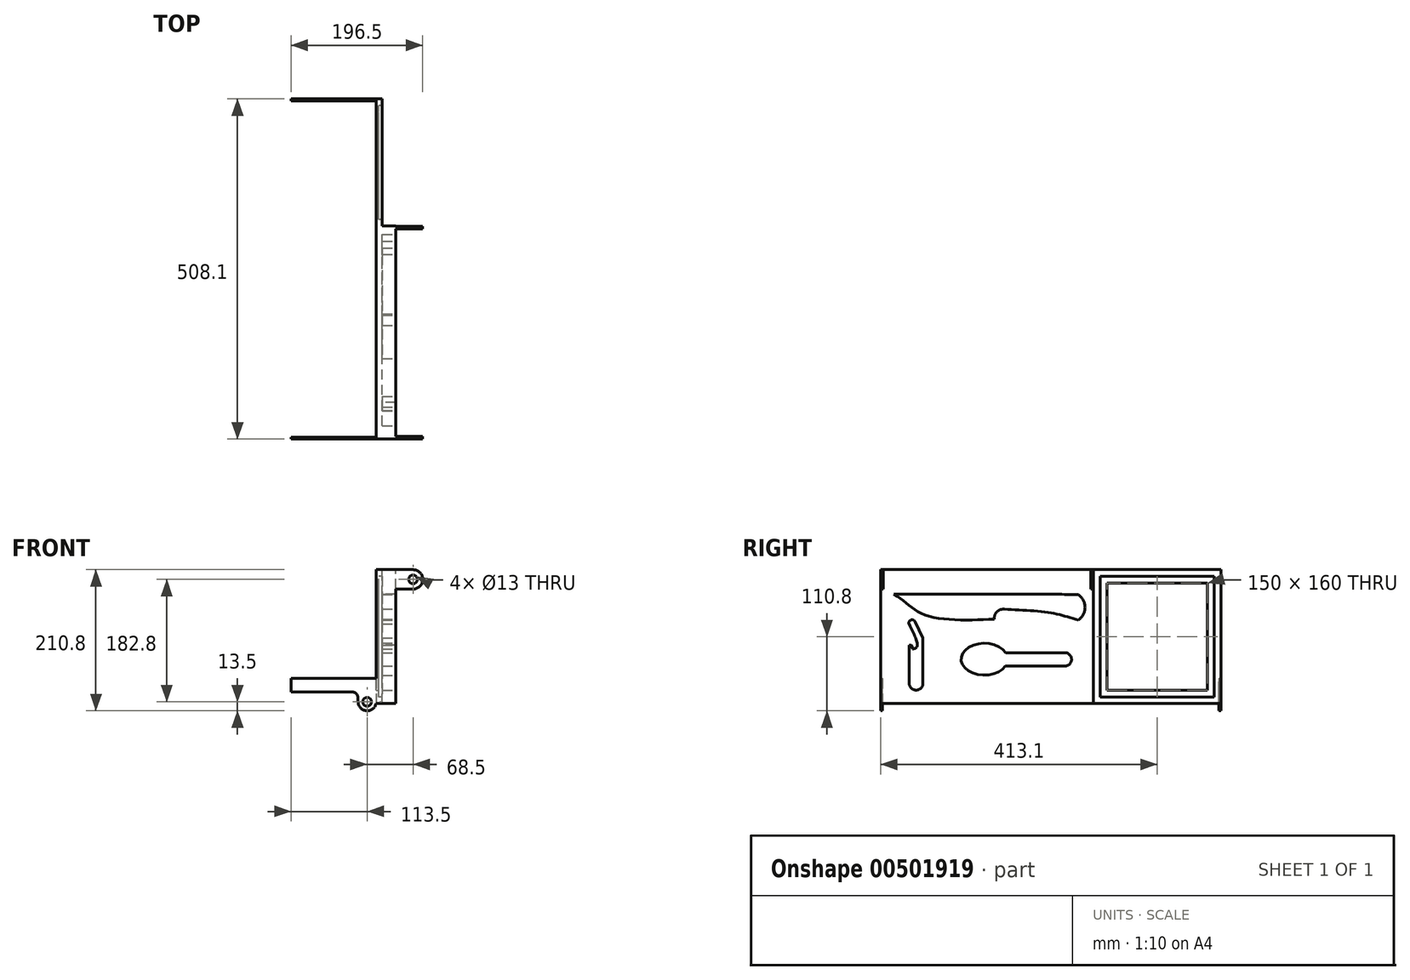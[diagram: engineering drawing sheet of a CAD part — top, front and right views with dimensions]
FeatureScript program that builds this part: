
annotation { "Feature Type Name" : "Feature", "Feature Type Description" : "" }
export const myFeature = defineFeature(function(context is Context, id is Id, definition is map)
    precondition{}
    {
        {
            var Q0;
            Q0=qCreatedBy(makeId("Front.planeOp"),FACE);
            var sketch = newSketch(context, id + "F0", { "sketchPlane" : qUnion([Q0])});
            skArc(sketch, "E0", {"start": v(-13.5, 0) * mm, "mid": v(-1.36, -13.43) * mm, "end": v(13.23, -2.7) * mm});
            skLineSegment(sketch, "E1.left", {"start": v(-13.5, 0) * mm, "end": v(-13.5, 15) * mm});
            skLineSegment(sketch, "E1.right", {"start": v(13.5, -2.7) * mm, "end": v(13.5, 15) * mm});
            skLineSegment(sketch, "E2.trimOffspring", {"start": v(13.23, -2.7) * mm, "end": v(13.5, -2.7) * mm});
            skLineSegment(sketch, "E3.bottom", {"start": v(-13.5, 15) * mm, "end": v(-113.5, 15) * mm});
            skLineSegment(sketch, "E3.top", {"start": v(13.5, 35) * mm, "end": v(-113.5, 35) * mm});
            skLineSegment(sketch, "E3.left", {"start": v(13.5, 15) * mm, "end": v(13.5, 35) * mm});
            skLineSegment(sketch, "E3.right", {"start": v(-113.5, 15) * mm, "end": v(-113.5, 35) * mm});
            skPoint(sketch, "E4.start.orphan", {"position": v(-6.5, 0) * mm});
            skPoint(sketch, "E5.end.orphan", {"position": v(6.5, 0) * mm});
            skCircle(sketch, "E6", {"center": v(0, 0) * mm, "radius": 6.5 * mm});
            skSolve(sketch);
        }
        {
            var Q0;
            Q0=makeQuery(id+"F0.imprint","IMPRINT",FACE,{"disambiguationData":[TD([[makeQuery(id+"F0.imprint","IMPRINT",EDGE,{"derivedFrom":sQuery(id+"F0.wireOp",EDGE,"E0")}),1.0]])]});
            extrude(context, id + "F1", {"entities" : qUnion([Q0]), "endBound" : BoundingType.SYMMETRIC, "depth" : 508.1 * mm});
        }
        {
            var Q0;
            Q0=makeQuery(id+"F1.opExtrude","SWEPT_FACE",FACE,{"disambiguationData":[OSD([sQuery(id+"F0.wireOp",EDGE,"E1.right"),sQuery(id+"F0.wireOp",EDGE,"E3.left")])]});
            var sketch = newSketch(context, id + "F2", { "sketchPlane" : qUnion([Q0])});
            skLineSegment(sketch, "E7.bottom", {"start": v(-251.05, 50) * mm, "end": v(251.05, 50) * mm});
            skLineSegment(sketch, "E7.top", {"start": v(-251.05, -50) * mm, "end": v(251.05, -50) * mm});
            skLineSegment(sketch, "E7.left", {"start": v(-251.05, 50) * mm, "end": v(-251.05, -50) * mm});
            skLineSegment(sketch, "E7.right", {"start": v(251.05, 50) * mm, "end": v(251.05, -50) * mm});
            skPoint(sketch, "E7.middle", {"position": v(0, 0) * mm});
            skSolve(sketch);
        }
        {
            var Q0;
            Q0=qSketchRegion(id+"F2",true);
            extrude(context, id + "F3", {"entities" : qUnion([Q0]), "operationType" : NewBodyOperationType.REMOVE, "oppositeDirection" : true, "depth" : 140 * mm});
        }
        {
            var Q0;
            {var subQ0=sQuery(id+"F0.wireOp",EDGE,"E3.bottom");var subQ1=sQuery(id+"F0.wireOp",EDGE,"E1.left");Q0=makeQuery(id+"F3.boolean.opBoolean","SPLIT",EDGE,{"disambiguationData":[TD([makeQuery(id+"F3.opExtrude","SWEPT_FACE",FACE,{"disambiguationData":[OSD([sQuery(id+"F2.wireOp",EDGE,"E7.left")])]})])],"derivedFrom":makeQuery(id+"F1.opExtrude","SWEPT_EDGE",EDGE,{"disambiguationData":[OSD([subQ1,subQ0])]})});}
            var Q1;
            {var subQ0=sQuery(id+"F0.wireOp",EDGE,"E3.bottom");var subQ1=sQuery(id+"F0.wireOp",EDGE,"E1.left");Q1=makeQuery(id+"F3.boolean.opBoolean","SPLIT",EDGE,{"disambiguationData":[TD([makeQuery(id+"F3.opExtrude","SWEPT_FACE",FACE,{"disambiguationData":[OSD([sQuery(id+"F2.wireOp",EDGE,"E7.right")])]})])],"derivedFrom":makeQuery(id+"F1.opExtrude","SWEPT_EDGE",EDGE,{"disambiguationData":[OSD([subQ1,subQ0])]})});}
            fillet(context, id + "F4", {"entities" : qUnion([Q0, Q1]), "radius" : 10 * mm, "tangentPropagation" : true, "allowEdgeOverflow" : false});
        }
        {
            var Q0;
            {var subQ0=sQuery(id+"F0.wireOp",EDGE,"E3.left");var subQ3=sQuery(id+"F0.wireOp",EDGE,"E1.right");Q0=makeQuery(id+"F3.boolean.opBoolean","SPLIT",FACE,{"disambiguationData":[TD([makeQuery(id+"F3.opExtrude","SWEPT_FACE",FACE,{"disambiguationData":[OSD([sQuery(id+"F2.wireOp",EDGE,"E7.left")])]})])],"derivedFrom":makeQuery(id+"F1.opExtrude","SWEPT_FACE",FACE,{"disambiguationData":[OSD([subQ3,subQ0])]})});}
            var sketch = newSketch(context, id + "F5", { "sketchPlane" : qUnion([Q0])});
            skLineSegment(sketch, "E8.bottom", {"start": v(-254.05, -2.7) * mm, "end": v(254.05, -2.7) * mm});
            skLineSegment(sketch, "E8.top", {"start": v(-254.05, 197.3) * mm, "end": v(254.05, 197.3) * mm});
            skLineSegment(sketch, "E8.left", {"start": v(-254.05, -2.7) * mm, "end": v(-254.05, 197.3) * mm});
            skLineSegment(sketch, "E8.right", {"start": v(254.05, -2.7) * mm, "end": v(254.05, 197.3) * mm});
            skSolve(sketch);
        }
        {
            var Q0;
            Q0=qSketchRegion(id+"F5",true);
            extrude(context, id + "F6", {"entities" : qUnion([Q0]), "operationType" : NewBodyOperationType.ADD, "depth" : 4 * mm});
        }
        {
            var Q0;
            Q0=makeQuery(id+"F6.opExtrude","CAP_FACE",FACE,{"disambiguationData":[OSD([sQuery(id+"F5.wireOp",EDGE,"E8.bottom"),sQuery(id+"F5.wireOp",EDGE,"E8.top"),sQuery(id+"F5.wireOp",EDGE,"E8.left"),sQuery(id+"F5.wireOp",EDGE,"E8.right")])],"isStart":false});
            var sketch = newSketch(context, id + "F7", { "sketchPlane" : qUnion([Q0])});
            skLineSegment(sketch, "E9.bottom", {"start": v(84.05, 17.3) * mm, "end": v(234.05, 17.3) * mm});
            skLineSegment(sketch, "E9.top", {"start": v(84.05, 177.3) * mm, "end": v(234.05, 177.3) * mm});
            skLineSegment(sketch, "E9.left", {"start": v(84.05, 17.3) * mm, "end": v(84.05, 177.3) * mm});
            skLineSegment(sketch, "E9.right", {"start": v(234.05, 17.3) * mm, "end": v(234.05, 177.3) * mm});
            skSolve(sketch);
        }
        {
            var Q0;
            Q0 = qSketchRegion(id + "F7", true);
            extrude(context, id + "F8", {"entities" : qUnion([Q0]), "operationType" : NewBodyOperationType.REMOVE, "oppositeDirection" : true, "depth" : 25 * mm});
        }
        {
            var Q0;
            Q0=makeQuery(id+"F6.opExtrude","CAP_FACE",FACE,{"disambiguationData":[OSD([sQuery(id+"F5.wireOp",EDGE,"E8.bottom"),sQuery(id+"F5.wireOp",EDGE,"E8.top"),sQuery(id+"F5.wireOp",EDGE,"E8.left"),sQuery(id+"F5.wireOp",EDGE,"E8.right")])],"isStart":false});
            var sketch = newSketch(context, id + "F9", { "sketchPlane" : qUnion([Q0])});
            skLineSegment(sketch, "E10.bottom", {"start": v(254.05, -2.7) * mm, "end": v(64.05, -2.7) * mm});
            skLineSegment(sketch, "E10.top", {"start": v(254.05, 197.3) * mm, "end": v(64.05, 197.3) * mm});
            skLineSegment(sketch, "E10.left", {"start": v(254.05, -2.7) * mm, "end": v(254.05, 197.3) * mm});
            skLineSegment(sketch, "E10.right", {"start": v(64.05, -2.7) * mm, "end": v(64.05, 197.3) * mm});
            skSolve(sketch);
        }
        {
            var Q0;
            Q0 = qSketchRegion(id + "F9", true);
            extrude(context, id + "F10", {"entities" : qUnion([Q0]), "operationType" : NewBodyOperationType.ADD, "depth" : 5 * mm});
        }
        {
            var Q0;
            Q0=makeQuery(id+"F9.imprint","IMPRINT",FACE,{"disambiguationData":[TD([[makeQuery(id+"F9.imprint","IMPRINT",EDGE,{"derivedFrom":sQuery(id+"F9.wireOp",EDGE,"E10.bottom")}),1.0]])]});
            var sketch = newSketch(context, id + "F11", { "sketchPlane" : qUnion([Q0])});
            skLineSegment(sketch, "E11.bottom", {"start": v(74.05, 7.3) * mm, "end": v(244.05, 7.3) * mm});
            skLineSegment(sketch, "E11.top", {"start": v(74.05, 187.3) * mm, "end": v(244.05, 187.3) * mm});
            skLineSegment(sketch, "E11.left", {"start": v(74.05, 7.3) * mm, "end": v(74.05, 187.3) * mm});
            skLineSegment(sketch, "E11.right", {"start": v(244.05, 7.3) * mm, "end": v(244.05, 187.3) * mm});
            skSolve(sketch);
        }
        {
            var Q0;
            Q0 = qSketchRegion(id + "F11", true);
            extrude(context, id + "F12", {"entities" : qUnion([Q0]), "operationType" : NewBodyOperationType.REMOVE, "depth" : 25 * mm});
        }
        {
            var Q0;
            Q0=makeQuery(id+"F6.opExtrude","CAP_FACE",FACE,{"disambiguationData":[OSD([sQuery(id+"F5.wireOp",EDGE,"E8.bottom"),sQuery(id+"F5.wireOp",EDGE,"E8.top"),sQuery(id+"F5.wireOp",EDGE,"E8.left"),sQuery(id+"F5.wireOp",EDGE,"E8.right")])],"isStart":false});
            var sketch = newSketch(context, id + "F13", { "sketchPlane" : qUnion([Q0])});
            skLineSegment(sketch, "E12.bottom", {"start": v(-254.05, -2.7) * mm, "end": v(64.05, -2.7) * mm});
            skLineSegment(sketch, "E12.top", {"start": v(-254.05, 197.3) * mm, "end": v(64.05, 197.3) * mm});
            skLineSegment(sketch, "E12.left", {"start": v(-254.05, -2.7) * mm, "end": v(-254.05, 197.3) * mm});
            skLineSegment(sketch, "E12.right", {"start": v(64.05, -2.7) * mm, "end": v(64.05, 197.3) * mm});
            skSolve(sketch);
        }
        {
            var Q0;
            Q0 = qSketchRegion(id + "F13", true);
            extrude(context, id + "F14", {"entities" : qUnion([Q0]), "operationType" : NewBodyOperationType.ADD, "depth" : 25 * mm});
        }
        {
            var Q0;
            Q0=makeQuery(id+"F14.opExtrude","CAP_FACE",FACE,{"disambiguationData":[OSD([sQuery(id+"F13.wireOp",EDGE,"E12.bottom"),sQuery(id+"F13.wireOp",EDGE,"E12.top"),sQuery(id+"F13.wireOp",EDGE,"E12.left"),sQuery(id+"F13.wireOp",EDGE,"E12.right")])],"isStart":false});
            var sketch = newSketch(context, id + "F15", { "sketchPlane" : qUnion([Q0])});
            skLineSegment(sketch, "E13", {"start": v(-234.06, 160.84) * mm, "end": v(-42.72, 160.84) * mm});
            skFitSpline(sketch, "E14", {"points": [v(-234.06, 160.84) * mm, v(-190.52, 130.77) * mm, v(-84.33, 123.56) * mm], "startDerivative": vector(123, -69.12) * mm, "endDerivative": vector(178.86, 10.6) * mm});
            skArc(sketch, "E15", {"start": v(-69.13, 138.37) * mm, "mid": v(-80.08, 134.4) * mm, "end": v(-84.33, 123.56) * mm});
            skFitSpline(sketch, "E16", {"points": [v(-69.13, 138.37) * mm, v(0, 132.93) * mm, v(41.5, 122.18) * mm], "startDerivative": vector(118.54, -7.26) * mm, "endDerivative": vector(102.56, -27.5) * mm});
            skArc(sketch, "E17", {"start": v(41.5, 122.18) * mm, "mid": v(51.42, 141) * mm, "end": v(41.5, 159.82) * mm});
            skFitSpline(sketch, "E18", {"points": [v(-42.72, 160.84) * mm, v(0, 160.84) * mm, v(41.5, 159.82) * mm], "startDerivative": vector(93.42, 0.52) * mm, "endDerivative": vector(74.55, -2.22) * mm});
            skEllipticalArc(sketch, "E19", {});
            skLineSegment(sketch, "E20.bottom", {"start": v(21.55, 73.4) * mm, "end": v(-67.06, 73.4) * mm});
            skLineSegment(sketch, "E20.top", {"start": v(21.16, 53.32) * mm, "end": v(-67.45, 53.32) * mm});
            skArc(sketch, "E21", {"start": v(21.16, 53.32) * mm, "mid": v(31.2, 63.17) * mm, "end": v(21.55, 73.4) * mm});
            skLineSegment(sketch, "E22.left", {"start": v(-190.6, 27.77) * mm, "end": v(-190.6, 78.62) * mm});
            skLineSegment(sketch, "E22.right", {"start": v(-211.16, 27.77) * mm, "end": v(-211.16, 78.62) * mm});
            skPoint(sketch, "E22.middle", {"position": v(-200.88, 53.2) * mm});
            skArc(sketch, "E23", {"start": v(-211.16, 27.77) * mm, "mid": v(-200.88, 17.48) * mm, "end": v(-190.6, 27.77) * mm});
            skLineSegment(sketch, "E24", {"start": v(-190.6, 78.62) * mm, "end": v(-190.6, 95.2) * mm});
            skLineSegment(sketch, "E25", {"start": v(-190.6, 95.2) * mm, "end": v(-202.45, 119.74) * mm});
            skLineSegment(sketch, "E26", {"start": v(-211.16, 78.62) * mm, "end": v(-211.16, 84.5) * mm});
            skFitSpline(sketch, "E27", {"points": [v(-206.3, 78.62) * mm, v(-199.26, 82.66) * mm, v(-211.44, 116.07) * mm], "startDerivative": vector(28.24, 6.55) * mm, "endDerivative": vector(-31.47, 61.86) * mm});
            skFitSpline(sketch, "E28", {"points": [v(-211.16, 84.5) * mm, v(-207.87, 84.5) * mm, v(-206.3, 78.62) * mm], "startDerivative": vector(8.84, 2.16) * mm, "endDerivative": vector(1.25, -13.15) * mm});
            skArc(sketch, "E29", {"start": v(-202.45, 119.74) * mm, "mid": v(-208.66, 122.13) * mm, "end": v(-211.44, 116.07) * mm});
            const initialGuessF15  = {"E19": [-0.09883789050244385, 0.06364599973239364, 1, 0, 0.03481733814341265, 0.02387090292371184, 0.4207699255388472, 5.835743280041866]};
            skSetInitialGuess(sketch, initialGuessF15);
            skSolve(sketch);
        }
        {
            var Q0;
            Q0 = qSketchRegion(id + "F15", true);
            extrude(context, id + "F16", {"entities" : qUnion([Q0]), "operationType" : NewBodyOperationType.REMOVE, "oppositeDirection" : true, "depth" : 20 * mm});
        }
        {
            var Q0;
            Q0=makeQuery(id+"F14.boolean.opBoolean","MERGE",FACE,{"derivedFrom":[makeQuery(id+"F6.boolean.opBoolean","MERGE",FACE,{"derivedFrom":[makeQuery(id+"F1.opExtrude","CAP_FACE",FACE,{"disambiguationData":[OSD([sQuery(id+"F0.wireOp",EDGE,"E0"),sQuery(id+"F0.wireOp",EDGE,"E1.left"),sQuery(id+"F0.wireOp",EDGE,"E1.right"),sQuery(id+"F0.wireOp",EDGE,"E2.trimOffspring"),sQuery(id+"F0.wireOp",EDGE,"E3.bottom"),sQuery(id+"F0.wireOp",EDGE,"E3.top"),sQuery(id+"F0.wireOp",EDGE,"E3.left"),sQuery(id+"F0.wireOp",EDGE,"E3.right"),sQuery(id+"F0.wireOp",EDGE,"E6")])],"isStart":false}),makeQuery(id+"F6.opExtrude","SWEPT_FACE",FACE,{"disambiguationData":[OSD([sQuery(id+"F5.wireOp",EDGE,"E8.left")])]})]}),makeQuery(id+"F14.opExtrude","SWEPT_FACE",FACE,{"disambiguationData":[OSD([sQuery(id+"F13.wireOp",EDGE,"E12.left")])]})]});
            var sketch = newSketch(context, id + "F17", { "sketchPlane" : qUnion([Q0])});
            skLineSegment(sketch, "E30.bottom", {"start": v(42.5, 197.3) * mm, "end": v(68.5, 197.3) * mm});
            skLineSegment(sketch, "E30.top", {"start": v(42.5, 168.3) * mm, "end": v(68.5, 168.3) * mm});
            skLineSegment(sketch, "E30.left", {"start": v(42.5, 197.3) * mm, "end": v(42.5, 168.3) * mm});
            skArc(sketch, "E31", {"start": v(68.5, 168.3) * mm, "mid": v(83, 182.8) * mm, "end": v(68.5, 197.3) * mm});
            skCircle(sketch, "E32", {"center": v(68.5, 182.8) * mm, "radius": 6.5 * mm});
            skSolve(sketch);
        }
        {
            var Q0;
            Q0 = qSketchRegion(id + "F17", true);
            extrude(context, id + "F18", {"entities" : qUnion([Q0]), "operationType" : NewBodyOperationType.ADD, "oppositeDirection" : true, "depth" : 318 * mm});
        }
        {
            var Q0;
            Q0=makeQuery(id+"F18.boolean.opBoolean","MERGE",FACE,{"derivedFrom":[makeQuery(id+"F14.boolean.opBoolean","MERGE",FACE,{"derivedFrom":[makeQuery(id+"F10.boolean.opBoolean","MERGE",FACE,{"derivedFrom":[makeQuery(id+"F6.opExtrude","SWEPT_FACE",FACE,{"disambiguationData":[OSD([sQuery(id+"F5.wireOp",EDGE,"E8.top")])]}),makeQuery(id+"F10.opExtrude","SWEPT_FACE",FACE,{"disambiguationData":[OSD([sQuery(id+"F9.wireOp",EDGE,"E10.top")])]})]}),makeQuery(id+"F14.opExtrude","SWEPT_FACE",FACE,{"disambiguationData":[OSD([sQuery(id+"F13.wireOp",EDGE,"E12.top")])]})]}),makeQuery(id+"F18.opExtrude","SWEPT_FACE",FACE,{"disambiguationData":[OSD([sQuery(id+"F17.wireOp",EDGE,"E30.bottom")])]})]});
            var sketch = newSketch(context, id + "F19", { "sketchPlane" : qUnion([Q0])});
            skLineSegment(sketch, "E33.bottom", {"start": v(42.5, 59.95) * mm, "end": v(94.5, 59.95) * mm});
            skLineSegment(sketch, "E33.top", {"start": v(42.5, -250.05) * mm, "end": v(94.5, -250.05) * mm});
            skLineSegment(sketch, "E33.left", {"start": v(42.5, 59.95) * mm, "end": v(42.5, -250.05) * mm});
            skLineSegment(sketch, "E33.right", {"start": v(94.5, 59.95) * mm, "end": v(94.5, -250.05) * mm});
            skPoint(sketch, "E33.middle", {"position": v(68.5, -95.05) * mm});
            skSolve(sketch);
        }
        {
            var Q0;
            Q0 = qSketchRegion(id + "F19", true);
            extrude(context, id + "F20", {"entities" : qUnion([Q0]), "operationType" : NewBodyOperationType.REMOVE, "oppositeDirection" : true, "depth" : 30 * mm});
        }
    });
